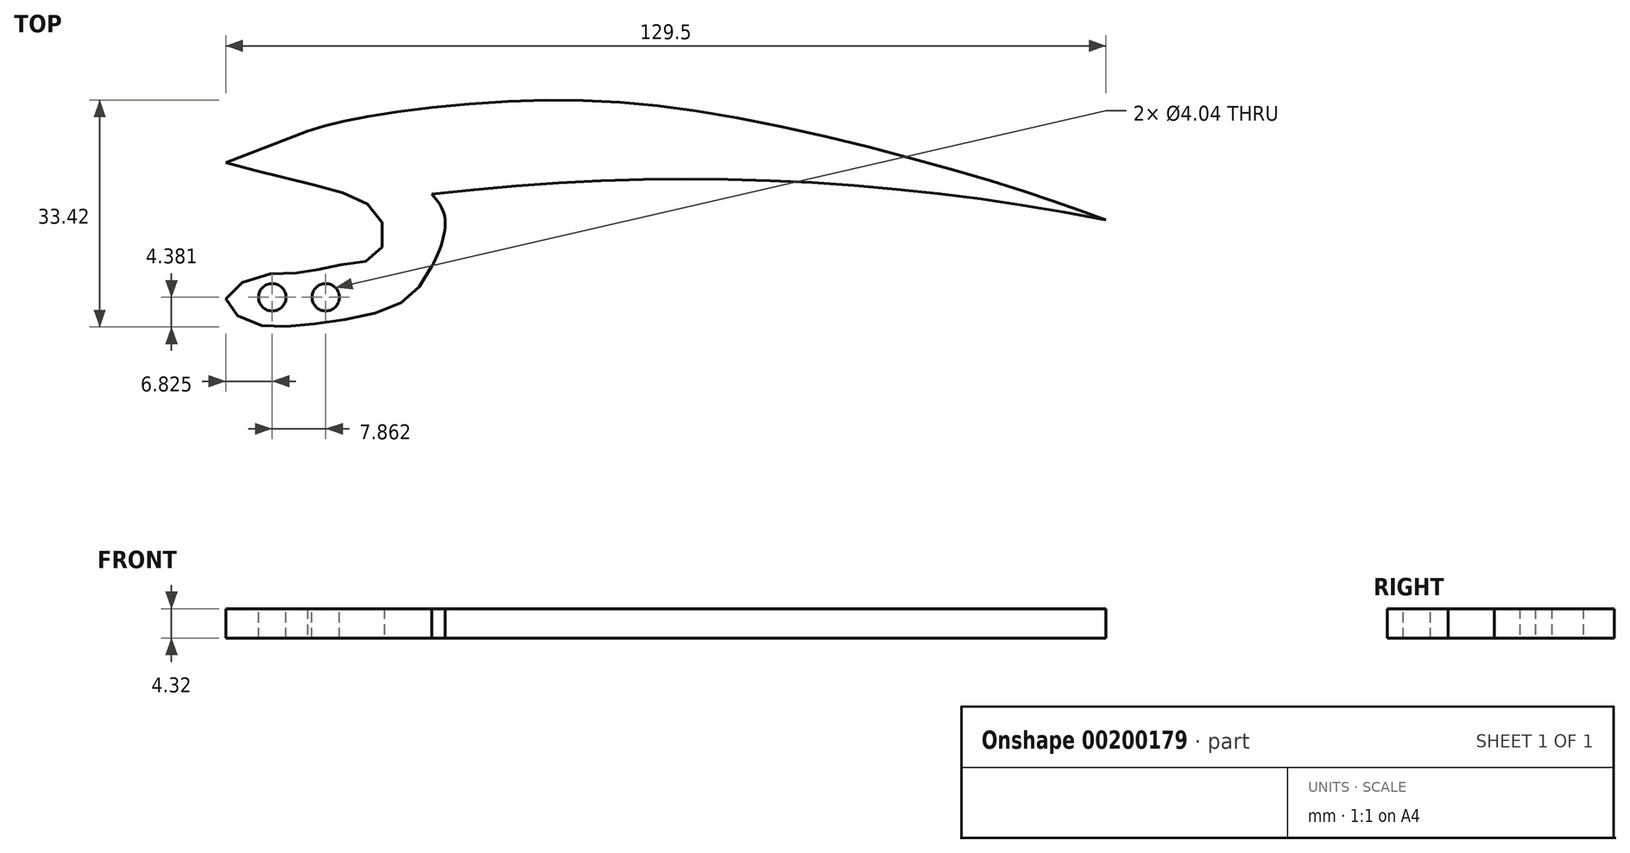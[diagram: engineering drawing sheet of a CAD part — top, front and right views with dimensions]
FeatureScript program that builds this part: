
annotation { "Feature Type Name" : "Feature", "Feature Type Description" : "" }
export const myFeature = defineFeature(function(context is Context, id is Id, definition is map)
    precondition{}
    {
        {
            var Q0;
            Q0=qCreatedBy(makeId("Top.planeOp"),FACE);
            var sketch = newSketch(context, id + "F0", { "sketchPlane" : qUnion([Q0])});
            skFitSpline(sketch, "E0", {"points": [v(-32.73, 9.32) * mm, v(-24.84, 11.3) * mm, v(0, 13.8) * mm, v(29.15, 11.48) * mm, v(66.63, 2.33) * mm, v(84.75, -3.77) * mm], "startDerivative": vector(55.7, 16.58) * mm, "endDerivative": vector(87.5, -31.61) * mm});
            skFitSpline(sketch, "E1", {"points": [v(-32.73, 9.32) * mm, v(-44.75, 4.66) * mm], "startDerivative": vector(-12.02, -4.66) * mm, "endDerivative": vector(-12.02, -4.66) * mm});
            skFitSpline(sketch, "E2", {"points": [v(-44.75, 4.66) * mm, v(-35.78, 2.33) * mm, v(-27, 0) * mm, v(-21.97, -3.59) * mm, v(-22.5, -8.97) * mm, v(-28.07, -10.4) * mm, v(-33.1, -11.48) * mm, v(-39.73, -12.02) * mm, v(-44.75, -15.6) * mm, v(-40.8, -19.01) * mm, v(-34.53, -19.37) * mm, v(-25.2, -18.12) * mm, v(-17.85, -15.25) * mm, v(-14.44, -10.58) * mm], "startDerivative": vector(98.34, -26.55) * mm, "endDerivative": vector(39.01, 71.8) * mm});
            skFitSpline(sketch, "E3", {"points": [v(-14.44, -10.58) * mm, v(-13, -7.36) * mm, v(-12.64, -2.87) * mm, v(-14.44, 0) * mm], "startDerivative": vector(4.88, 9.23) * mm, "endDerivative": vector(-7.13, 8.15) * mm});
            skArc(sketch, "E4", {"start": v(84.75, -3.77) * mm, "mid": v(35.3, 2) * mm, "end": v(-14.44, 0) * mm});
            skSolve(sketch);
        }
        {
            var Q0;
            Q0=makeQuery(id+"F0.imprint","IMPRINT",FACE,{"disambiguationData":[TD([[makeQuery(id+"F0.imprint","IMPRINT",EDGE,{"derivedFrom":sQuery(id+"F0.wireOp",EDGE,"E0")}),-1.0]])]});
            extrude(context, id + "F1", {"entities" : qUnion([Q0]), "depth" : 4.32 * mm});
        }
        {
            var Q0;
            Q0=makeQuery(id+"F1.opExtrude","CAP_FACE",FACE,{"disambiguationData":[OSD([sQuery(id+"F0.wireOp",EDGE,"E0"),sQuery(id+"F0.wireOp",EDGE,"E1"),sQuery(id+"F0.wireOp",EDGE,"E2"),sQuery(id+"F0.wireOp",EDGE,"E3"),sQuery(id+"F0.wireOp",EDGE,"E4")])],"isStart":false});
            var sketch = newSketch(context, id + "F2", { "sketchPlane" : qUnion([Q0])});
            skCircle(sketch, "E5", {"center": v(-37.93, -15.17) * mm, "radius": 2.02 * mm});
            skCircle(sketch, "E6", {"center": v(-30.06, -15.17) * mm, "radius": 2.02 * mm});
            skSolve(sketch);
        }
        {
            var Q0;
            Q0=makeQuery(id+"F2.imprint","IMPRINT",FACE,{"disambiguationData":[TD([[makeQuery(id+"F2.imprint","IMPRINT",EDGE,{"derivedFrom":sQuery(id+"F2.wireOp",EDGE,"E5")}),1.0]])]});
            var Q1;
            Q1=makeQuery(id+"F2.imprint","IMPRINT",FACE,{"disambiguationData":[TD([[makeQuery(id+"F2.imprint","IMPRINT",EDGE,{"derivedFrom":sQuery(id+"F2.wireOp",EDGE,"E6")}),1.0]])]});
            extrude(context, id + "F3", {"entities" : qUnion([Q0, Q1]), "operationType" : NewBodyOperationType.REMOVE, "oppositeDirection" : true, "depth" : 43.18 * mm});
        }
    });
